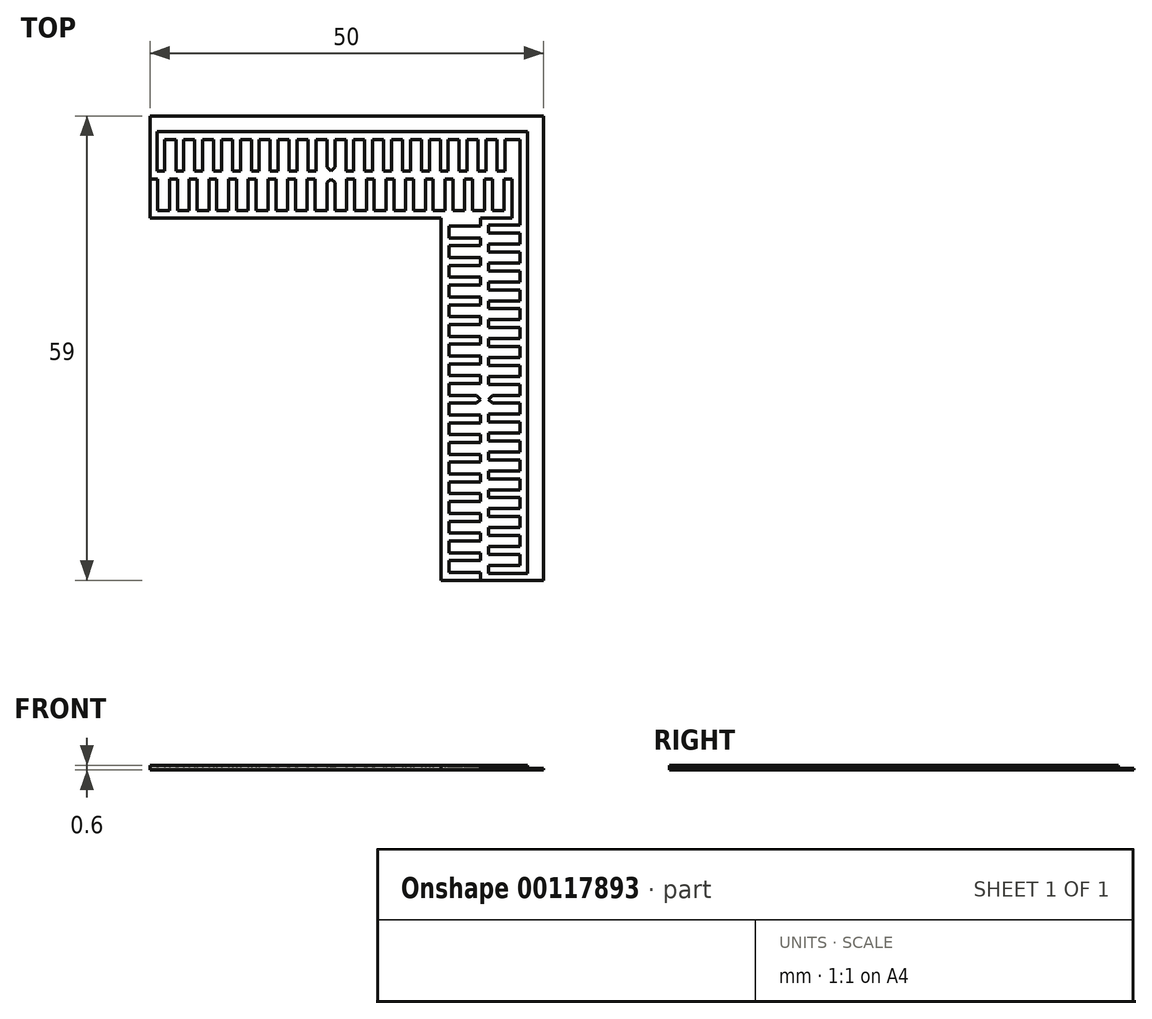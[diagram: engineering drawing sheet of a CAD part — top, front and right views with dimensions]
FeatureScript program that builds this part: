
annotation { "Feature Type Name" : "Feature", "Feature Type Description" : "" }
export const myFeature = defineFeature(function(context is Context, id is Id, definition is map)
    precondition{}
    {
        {
            assignVariable(context, id + "F0", {"name" : "pegThickness", "anyValue" : 0.4});
        }
        {
            var Q0;
            Q0=qCreatedBy(makeId("Top.planeOp"),FACE);
            var sketch = newSketch(context, id + "F1", { "sketchPlane" : qUnion([Q0])});
            skLineSegment(sketch, "E0.bottom", {"start": v(-0.5, 4) * mm, "end": v(0.5, 4) * mm});
            skLineSegment(sketch, "E0.top", {"start": v(-0.5, 0) * mm, "end": v(0.5, 0) * mm});
            skLineSegment(sketch, "E0.left", {"start": v(-0.5, 4) * mm, "end": v(-0.5, 0) * mm});
            skLineSegment(sketch, "E0.right", {"start": v(0.5, 4) * mm, "end": v(0.5, 0) * mm});
            skLineSegment(sketch, "E1.1.0.0", {"start": v(2, 0) * mm, "end": v(3, 0) * mm});
            skLineSegment(sketch, "E1.1.0.1", {"start": v(2, 4) * mm, "end": v(2, 0) * mm});
            skLineSegment(sketch, "E1.1.0.2", {"start": v(3, 4) * mm, "end": v(3, 0) * mm});
            skLineSegment(sketch, "E1.1.0.3", {"start": v(2, 4) * mm, "end": v(3, 4) * mm});
            skLineSegment(sketch, "E1.2.0.0", {"start": v(4.5, 0) * mm, "end": v(5.5, 0) * mm});
            skLineSegment(sketch, "E1.2.0.1", {"start": v(4.5, 4) * mm, "end": v(4.5, 0) * mm});
            skLineSegment(sketch, "E1.2.0.2", {"start": v(5.5, 4) * mm, "end": v(5.5, 0) * mm});
            skLineSegment(sketch, "E1.2.0.3", {"start": v(4.5, 4) * mm, "end": v(5.5, 4) * mm});
            skLineSegment(sketch, "E1.3.0.0", {"start": v(7, 0) * mm, "end": v(8, 0) * mm});
            skLineSegment(sketch, "E1.3.0.1", {"start": v(7, 4) * mm, "end": v(7, 0) * mm});
            skLineSegment(sketch, "E1.3.0.2", {"start": v(8, 4) * mm, "end": v(8, 0) * mm});
            skLineSegment(sketch, "E1.3.0.3", {"start": v(7, 4) * mm, "end": v(8, 4) * mm});
            skLineSegment(sketch, "E1.4.0.0", {"start": v(9.5, 0) * mm, "end": v(10.5, 0) * mm});
            skLineSegment(sketch, "E1.4.0.1", {"start": v(9.5, 4) * mm, "end": v(9.5, 0) * mm});
            skLineSegment(sketch, "E1.4.0.2", {"start": v(10.5, 4) * mm, "end": v(10.5, 0) * mm});
            skLineSegment(sketch, "E1.4.0.3", {"start": v(9.5, 4) * mm, "end": v(10.5, 4) * mm});
            skLineSegment(sketch, "E1.5.0.0", {"start": v(12, 0) * mm, "end": v(13, 0) * mm});
            skLineSegment(sketch, "E1.5.0.1", {"start": v(12, 4) * mm, "end": v(12, 0) * mm});
            skLineSegment(sketch, "E1.5.0.2", {"start": v(13, 4) * mm, "end": v(13, 0) * mm});
            skLineSegment(sketch, "E1.5.0.3", {"start": v(12, 4) * mm, "end": v(13, 4) * mm});
            skLineSegment(sketch, "E1.6.0.0", {"start": v(14.5, 0) * mm, "end": v(15.5, 0) * mm});
            skLineSegment(sketch, "E1.6.0.1", {"start": v(14.5, 4) * mm, "end": v(14.5, 0) * mm});
            skLineSegment(sketch, "E1.6.0.2", {"start": v(15.5, 4) * mm, "end": v(15.5, 0) * mm});
            skLineSegment(sketch, "E1.6.0.3", {"start": v(14.5, 4) * mm, "end": v(15.5, 4) * mm});
            skLineSegment(sketch, "E1.7.0.0", {"start": v(17, 0) * mm, "end": v(18, 0) * mm});
            skLineSegment(sketch, "E1.7.0.1", {"start": v(17, 4) * mm, "end": v(17, 0) * mm});
            skLineSegment(sketch, "E1.7.0.2", {"start": v(18, 4) * mm, "end": v(18, 0) * mm});
            skLineSegment(sketch, "E1.7.0.3", {"start": v(17, 4) * mm, "end": v(18, 4) * mm});
            skLineSegment(sketch, "E1.8.0.0", {"start": v(19.5, 0) * mm, "end": v(20.5, 0) * mm});
            skLineSegment(sketch, "E1.8.0.1", {"start": v(19.5, 4) * mm, "end": v(19.5, 0) * mm});
            skLineSegment(sketch, "E1.8.0.2", {"start": v(20.5, 4) * mm, "end": v(20.5, 0) * mm});
            skLineSegment(sketch, "E1.8.0.3", {"start": v(19.5, 4) * mm, "end": v(20.5, 4) * mm});
            skLineSegment(sketch, "E1.9.0.0", {"start": v(22, 0) * mm, "end": v(23, 0) * mm});
            skLineSegment(sketch, "E1.9.0.1", {"start": v(22, 4) * mm, "end": v(22, 0) * mm});
            skLineSegment(sketch, "E1.9.0.2", {"start": v(23, 4) * mm, "end": v(23, 0) * mm});
            skLineSegment(sketch, "E1.9.0.3", {"start": v(22, 4) * mm, "end": v(23, 4) * mm});
            skLineSegment(sketch, "E1.direction1", {"start": v(-0.5, 0) * mm, "end": v(2, 0) * mm, "construction": true});
            skLineSegment(sketch, "E2.1.0.0", {"start": v(-2, 4) * mm, "end": v(-2, 0) * mm});
            skLineSegment(sketch, "E2.1.0.1", {"start": v(-3, 4) * mm, "end": v(-3, 0) * mm});
            skLineSegment(sketch, "E2.1.0.2", {"start": v(-3, 0) * mm, "end": v(-2, 0) * mm});
            skLineSegment(sketch, "E2.1.0.3", {"start": v(-3, 4) * mm, "end": v(-2, 4) * mm});
            skLineSegment(sketch, "E2.2.0.0", {"start": v(-4.5, 4) * mm, "end": v(-4.5, 0) * mm});
            skLineSegment(sketch, "E2.2.0.1", {"start": v(-5.5, 4) * mm, "end": v(-5.5, 0) * mm});
            skLineSegment(sketch, "E2.2.0.2", {"start": v(-5.5, 0) * mm, "end": v(-4.5, 0) * mm});
            skLineSegment(sketch, "E2.2.0.3", {"start": v(-5.5, 4) * mm, "end": v(-4.5, 4) * mm});
            skLineSegment(sketch, "E2.3.0.0", {"start": v(-7, 4) * mm, "end": v(-7, 0) * mm});
            skLineSegment(sketch, "E2.3.0.1", {"start": v(-8, 4) * mm, "end": v(-8, 0) * mm});
            skLineSegment(sketch, "E2.3.0.2", {"start": v(-8, 0) * mm, "end": v(-7, 0) * mm});
            skLineSegment(sketch, "E2.3.0.3", {"start": v(-8, 4) * mm, "end": v(-7, 4) * mm});
            skLineSegment(sketch, "E2.4.0.0", {"start": v(-9.5, 4) * mm, "end": v(-9.5, 0) * mm});
            skLineSegment(sketch, "E2.4.0.1", {"start": v(-10.5, 4) * mm, "end": v(-10.5, 0) * mm});
            skLineSegment(sketch, "E2.4.0.2", {"start": v(-10.5, 0) * mm, "end": v(-9.5, 0) * mm});
            skLineSegment(sketch, "E2.4.0.3", {"start": v(-10.5, 4) * mm, "end": v(-9.5, 4) * mm});
            skLineSegment(sketch, "E2.5.0.0", {"start": v(-12, 4) * mm, "end": v(-12, 0) * mm});
            skLineSegment(sketch, "E2.5.0.1", {"start": v(-13, 4) * mm, "end": v(-13, 0) * mm});
            skLineSegment(sketch, "E2.5.0.2", {"start": v(-13, 0) * mm, "end": v(-12, 0) * mm});
            skLineSegment(sketch, "E2.5.0.3", {"start": v(-13, 4) * mm, "end": v(-12, 4) * mm});
            skLineSegment(sketch, "E2.6.0.0", {"start": v(-14.5, 4) * mm, "end": v(-14.5, 0) * mm});
            skLineSegment(sketch, "E2.6.0.1", {"start": v(-15.5, 4) * mm, "end": v(-15.5, 0) * mm});
            skLineSegment(sketch, "E2.6.0.2", {"start": v(-15.5, 0) * mm, "end": v(-14.5, 0) * mm});
            skLineSegment(sketch, "E2.6.0.3", {"start": v(-15.5, 4) * mm, "end": v(-14.5, 4) * mm});
            skLineSegment(sketch, "E2.7.0.0", {"start": v(-17, 4) * mm, "end": v(-17, 0) * mm});
            skLineSegment(sketch, "E2.7.0.1", {"start": v(-18, 4) * mm, "end": v(-18, 0) * mm});
            skLineSegment(sketch, "E2.7.0.2", {"start": v(-18, 0) * mm, "end": v(-17, 0) * mm});
            skLineSegment(sketch, "E2.7.0.3", {"start": v(-18, 4) * mm, "end": v(-17, 4) * mm});
            skLineSegment(sketch, "E2.8.0.0", {"start": v(-19.5, 4) * mm, "end": v(-19.5, 0) * mm});
            skLineSegment(sketch, "E2.8.0.1", {"start": v(-20.5, 4) * mm, "end": v(-20.5, 0) * mm});
            skLineSegment(sketch, "E2.8.0.2", {"start": v(-20.5, 0) * mm, "end": v(-19.5, 0) * mm});
            skLineSegment(sketch, "E2.8.0.3", {"start": v(-20.5, 4) * mm, "end": v(-19.5, 4) * mm});
            skLineSegment(sketch, "E2.9.0.0", {"start": v(-22, 4) * mm, "end": v(-22, 0) * mm});
            skLineSegment(sketch, "E2.9.0.1", {"start": v(-23, 4) * mm, "end": v(-23, 0) * mm});
            skLineSegment(sketch, "E2.9.0.2", {"start": v(-23, 0) * mm, "end": v(-22, 0) * mm});
            skLineSegment(sketch, "E2.9.0.3", {"start": v(-23, 4) * mm, "end": v(-22, 4) * mm});
            skLineSegment(sketch, "E2.direction1", {"start": v(-0.5, 0) * mm, "end": v(-3, 0) * mm, "construction": true});
            skLineSegment(sketch, "E3.bottom", {"start": v(-23, 0) * mm, "end": v(23, 0) * mm});
            skLineSegment(sketch, "E3.top", {"start": v(-23, -1) * mm, "end": v(23, -1) * mm});
            skLineSegment(sketch, "E3.left", {"start": v(-23, 0) * mm, "end": v(-23, -1) * mm});
            skLineSegment(sketch, "E3.right", {"start": v(23, 0) * mm, "end": v(23, -1) * mm});
            skSolve(sketch);
        }
        {
            var Q0;
            Q0=qSketchRegion(id+"F1",true);
            extrude(context, id + "F2", {"entities" : qUnion([Q0]), "depth" : (getVariable(context, 'pegThickness')) * mm});
        }
        {
            var Q0;
            Q0=qCreatedBy(makeId("Top.planeOp"),FACE);
            var sketch = newSketch(context, id + "F3", { "sketchPlane" : qUnion([Q0])});
            skLineSegment(sketch, "E4.bottom", {"start": v(-0.5, -5) * mm, "end": v(0.5, -5) * mm});
            skLineSegment(sketch, "E4.top", {"start": v(-0.5, -9) * mm, "end": v(0.5, -9) * mm});
            skLineSegment(sketch, "E4.left", {"start": v(-0.5, -5) * mm, "end": v(-0.5, -9) * mm});
            skLineSegment(sketch, "E4.right", {"start": v(0.5, -5) * mm, "end": v(0.5, -9) * mm});
            skLineSegment(sketch, "E5.1.0.0", {"start": v(1.9, -9) * mm, "end": v(2.9, -9) * mm});
            skLineSegment(sketch, "E5.1.0.1", {"start": v(1.9, -5) * mm, "end": v(1.9, -9) * mm});
            skLineSegment(sketch, "E5.1.0.2", {"start": v(2.9, -5) * mm, "end": v(2.9, -9) * mm});
            skLineSegment(sketch, "E5.1.0.3", {"start": v(1.9, -5) * mm, "end": v(2.9, -5) * mm});
            skLineSegment(sketch, "E5.2.0.0", {"start": v(4.3, -9) * mm, "end": v(5.3, -9) * mm});
            skLineSegment(sketch, "E5.2.0.1", {"start": v(4.3, -5) * mm, "end": v(4.3, -9) * mm});
            skLineSegment(sketch, "E5.2.0.2", {"start": v(5.3, -5) * mm, "end": v(5.3, -9) * mm});
            skLineSegment(sketch, "E5.2.0.3", {"start": v(4.3, -5) * mm, "end": v(5.3, -5) * mm});
            skLineSegment(sketch, "E5.3.0.0", {"start": v(6.7, -9) * mm, "end": v(7.7, -9) * mm});
            skLineSegment(sketch, "E5.3.0.1", {"start": v(6.7, -5) * mm, "end": v(6.7, -9) * mm});
            skLineSegment(sketch, "E5.3.0.2", {"start": v(7.7, -5) * mm, "end": v(7.7, -9) * mm});
            skLineSegment(sketch, "E5.3.0.3", {"start": v(6.7, -5) * mm, "end": v(7.7, -5) * mm});
            skLineSegment(sketch, "E5.4.0.0", {"start": v(9.1, -9) * mm, "end": v(10.1, -9) * mm});
            skLineSegment(sketch, "E5.4.0.1", {"start": v(9.1, -5) * mm, "end": v(9.1, -9) * mm});
            skLineSegment(sketch, "E5.4.0.2", {"start": v(10.1, -5) * mm, "end": v(10.1, -9) * mm});
            skLineSegment(sketch, "E5.4.0.3", {"start": v(9.1, -5) * mm, "end": v(10.1, -5) * mm});
            skLineSegment(sketch, "E5.5.0.0", {"start": v(11.5, -9) * mm, "end": v(12.5, -9) * mm});
            skLineSegment(sketch, "E5.5.0.1", {"start": v(11.5, -5) * mm, "end": v(11.5, -9) * mm});
            skLineSegment(sketch, "E5.5.0.2", {"start": v(12.5, -5) * mm, "end": v(12.5, -9) * mm});
            skLineSegment(sketch, "E5.5.0.3", {"start": v(11.5, -5) * mm, "end": v(12.5, -5) * mm});
            skLineSegment(sketch, "E5.6.0.0", {"start": v(13.9, -9) * mm, "end": v(14.9, -9) * mm});
            skLineSegment(sketch, "E5.6.0.1", {"start": v(13.9, -5) * mm, "end": v(13.9, -9) * mm});
            skLineSegment(sketch, "E5.6.0.2", {"start": v(14.9, -5) * mm, "end": v(14.9, -9) * mm});
            skLineSegment(sketch, "E5.6.0.3", {"start": v(13.9, -5) * mm, "end": v(14.9, -5) * mm});
            skLineSegment(sketch, "E5.7.0.0", {"start": v(16.3, -9) * mm, "end": v(17.3, -9) * mm});
            skLineSegment(sketch, "E5.7.0.1", {"start": v(16.3, -5) * mm, "end": v(16.3, -9) * mm});
            skLineSegment(sketch, "E5.7.0.2", {"start": v(17.3, -5) * mm, "end": v(17.3, -9) * mm});
            skLineSegment(sketch, "E5.7.0.3", {"start": v(16.3, -5) * mm, "end": v(17.3, -5) * mm});
            skLineSegment(sketch, "E5.8.0.0", {"start": v(18.7, -9) * mm, "end": v(19.7, -9) * mm});
            skLineSegment(sketch, "E5.8.0.1", {"start": v(18.7, -5) * mm, "end": v(18.7, -9) * mm});
            skLineSegment(sketch, "E5.8.0.2", {"start": v(19.7, -5) * mm, "end": v(19.7, -9) * mm});
            skLineSegment(sketch, "E5.8.0.3", {"start": v(18.7, -5) * mm, "end": v(19.7, -5) * mm});
            skLineSegment(sketch, "E5.9.0.0", {"start": v(21.1, -9) * mm, "end": v(22.1, -9) * mm});
            skLineSegment(sketch, "E5.9.0.1", {"start": v(21.1, -5) * mm, "end": v(21.1, -9) * mm});
            skLineSegment(sketch, "E5.9.0.2", {"start": v(22.1, -5) * mm, "end": v(22.1, -9) * mm});
            skLineSegment(sketch, "E5.9.0.3", {"start": v(21.1, -5) * mm, "end": v(22.1, -5) * mm});
            skLineSegment(sketch, "E5.direction1", {"start": v(-0.5, -9) * mm, "end": v(1.9, -9) * mm, "construction": true});
            skLineSegment(sketch, "E6.1.0.0", {"start": v(-1.9, -5) * mm, "end": v(-1.9, -9) * mm});
            skLineSegment(sketch, "E6.1.0.1", {"start": v(-2.9, -5) * mm, "end": v(-2.9, -9) * mm});
            skLineSegment(sketch, "E6.1.0.2", {"start": v(-2.9, -9) * mm, "end": v(-1.9, -9) * mm});
            skLineSegment(sketch, "E6.1.0.3", {"start": v(-2.9, -5) * mm, "end": v(-1.9, -5) * mm});
            skLineSegment(sketch, "E6.2.0.0", {"start": v(-4.3, -5) * mm, "end": v(-4.3, -9) * mm});
            skLineSegment(sketch, "E6.2.0.1", {"start": v(-5.3, -5) * mm, "end": v(-5.3, -9) * mm});
            skLineSegment(sketch, "E6.2.0.2", {"start": v(-5.3, -9) * mm, "end": v(-4.3, -9) * mm});
            skLineSegment(sketch, "E6.2.0.3", {"start": v(-5.3, -5) * mm, "end": v(-4.3, -5) * mm});
            skLineSegment(sketch, "E6.3.0.0", {"start": v(-6.7, -5) * mm, "end": v(-6.7, -9) * mm});
            skLineSegment(sketch, "E6.3.0.1", {"start": v(-7.7, -5) * mm, "end": v(-7.7, -9) * mm});
            skLineSegment(sketch, "E6.3.0.2", {"start": v(-7.7, -9) * mm, "end": v(-6.7, -9) * mm});
            skLineSegment(sketch, "E6.3.0.3", {"start": v(-7.7, -5) * mm, "end": v(-6.7, -5) * mm});
            skLineSegment(sketch, "E6.4.0.0", {"start": v(-9.1, -5) * mm, "end": v(-9.1, -9) * mm});
            skLineSegment(sketch, "E6.4.0.1", {"start": v(-10.1, -5) * mm, "end": v(-10.1, -9) * mm});
            skLineSegment(sketch, "E6.4.0.2", {"start": v(-10.1, -9) * mm, "end": v(-9.1, -9) * mm});
            skLineSegment(sketch, "E6.4.0.3", {"start": v(-10.1, -5) * mm, "end": v(-9.1, -5) * mm});
            skLineSegment(sketch, "E6.5.0.0", {"start": v(-11.5, -5) * mm, "end": v(-11.5, -9) * mm});
            skLineSegment(sketch, "E6.5.0.1", {"start": v(-12.5, -5) * mm, "end": v(-12.5, -9) * mm});
            skLineSegment(sketch, "E6.5.0.2", {"start": v(-12.5, -9) * mm, "end": v(-11.5, -9) * mm});
            skLineSegment(sketch, "E6.5.0.3", {"start": v(-12.5, -5) * mm, "end": v(-11.5, -5) * mm});
            skLineSegment(sketch, "E6.6.0.0", {"start": v(-13.9, -5) * mm, "end": v(-13.9, -9) * mm});
            skLineSegment(sketch, "E6.6.0.1", {"start": v(-14.9, -5) * mm, "end": v(-14.9, -9) * mm});
            skLineSegment(sketch, "E6.6.0.2", {"start": v(-14.9, -9) * mm, "end": v(-13.9, -9) * mm});
            skLineSegment(sketch, "E6.6.0.3", {"start": v(-14.9, -5) * mm, "end": v(-13.9, -5) * mm});
            skLineSegment(sketch, "E6.7.0.0", {"start": v(-16.3, -5) * mm, "end": v(-16.3, -9) * mm});
            skLineSegment(sketch, "E6.7.0.1", {"start": v(-17.3, -5) * mm, "end": v(-17.3, -9) * mm});
            skLineSegment(sketch, "E6.7.0.2", {"start": v(-17.3, -9) * mm, "end": v(-16.3, -9) * mm});
            skLineSegment(sketch, "E6.7.0.3", {"start": v(-17.3, -5) * mm, "end": v(-16.3, -5) * mm});
            skLineSegment(sketch, "E6.8.0.0", {"start": v(-18.7, -5) * mm, "end": v(-18.7, -9) * mm});
            skLineSegment(sketch, "E6.8.0.1", {"start": v(-19.7, -5) * mm, "end": v(-19.7, -9) * mm});
            skLineSegment(sketch, "E6.8.0.2", {"start": v(-19.7, -9) * mm, "end": v(-18.7, -9) * mm});
            skLineSegment(sketch, "E6.8.0.3", {"start": v(-19.7, -5) * mm, "end": v(-18.7, -5) * mm});
            skLineSegment(sketch, "E6.9.0.0", {"start": v(-21.1, -5) * mm, "end": v(-21.1, -9) * mm});
            skLineSegment(sketch, "E6.9.0.1", {"start": v(-22.1, -5) * mm, "end": v(-22.1, -9) * mm});
            skLineSegment(sketch, "E6.9.0.2", {"start": v(-22.1, -9) * mm, "end": v(-21.1, -9) * mm});
            skLineSegment(sketch, "E6.9.0.3", {"start": v(-22.1, -5) * mm, "end": v(-21.1, -5) * mm});
            skLineSegment(sketch, "E6.direction1", {"start": v(-0.5, -9) * mm, "end": v(-2.9, -9) * mm, "construction": true});
            skLineSegment(sketch, "E7.bottom", {"start": v(-22.1, -9) * mm, "end": v(22.1, -9) * mm});
            skLineSegment(sketch, "E7.top", {"start": v(-22.1, -10) * mm, "end": v(22.1, -10) * mm});
            skLineSegment(sketch, "E7.left", {"start": v(-22.1, -9) * mm, "end": v(-22.1, -10) * mm});
            skLineSegment(sketch, "E7.right", {"start": v(22.1, -9) * mm, "end": v(22.1, -10) * mm});
            skPoint(sketch, "E8", {"position": v(0, -5) * mm});
            skSolve(sketch);
        }
        {
            var Q0;
            Q0=qSketchRegion(id+"F3",true);
            extrude(context, id + "F4", {"entities" : qUnion([Q0]), "depth" : (getVariable(context, 'pegThickness')) * mm});
        }
        {
            var Q0;
            Q0=makeQuery(id+"F4.opExtrude","SWEPT_BODY",BODY,{"disambiguationData":[OSD([sQuery(id+"F3.wireOp",EDGE,"E4.bottom"),sQuery(id+"F3.wireOp",EDGE,"E4.left"),sQuery(id+"F3.wireOp",EDGE,"E4.right"),sQuery(id+"F3.wireOp",EDGE,"E5.1.0.1"),sQuery(id+"F3.wireOp",EDGE,"E5.1.0.2"),sQuery(id+"F3.wireOp",EDGE,"E5.1.0.3"),sQuery(id+"F3.wireOp",EDGE,"E5.2.0.1"),sQuery(id+"F3.wireOp",EDGE,"E5.2.0.2"),sQuery(id+"F3.wireOp",EDGE,"E5.2.0.3"),sQuery(id+"F3.wireOp",EDGE,"E5.3.0.1"),sQuery(id+"F3.wireOp",EDGE,"E5.3.0.2"),sQuery(id+"F3.wireOp",EDGE,"E5.3.0.3"),sQuery(id+"F3.wireOp",EDGE,"E5.4.0.1"),sQuery(id+"F3.wireOp",EDGE,"E5.4.0.2"),sQuery(id+"F3.wireOp",EDGE,"E5.4.0.3"),sQuery(id+"F3.wireOp",EDGE,"E5.5.0.1"),sQuery(id+"F3.wireOp",EDGE,"E5.5.0.2"),sQuery(id+"F3.wireOp",EDGE,"E5.5.0.3"),sQuery(id+"F3.wireOp",EDGE,"E5.6.0.1"),sQuery(id+"F3.wireOp",EDGE,"E5.6.0.2"),sQuery(id+"F3.wireOp",EDGE,"E5.6.0.3"),sQuery(id+"F3.wireOp",EDGE,"E5.7.0.1"),sQuery(id+"F3.wireOp",EDGE,"E5.7.0.2"),sQuery(id+"F3.wireOp",EDGE,"E5.7.0.3"),sQuery(id+"F3.wireOp",EDGE,"E5.8.0.1"),sQuery(id+"F3.wireOp",EDGE,"E5.8.0.2"),sQuery(id+"F3.wireOp",EDGE,"E5.8.0.3"),sQuery(id+"F3.wireOp",EDGE,"E5.9.0.1"),sQuery(id+"F3.wireOp",EDGE,"E5.9.0.2"),sQuery(id+"F3.wireOp",EDGE,"E5.9.0.3"),sQuery(id+"F3.wireOp",EDGE,"E6.1.0.0"),sQuery(id+"F3.wireOp",EDGE,"E6.1.0.1"),sQuery(id+"F3.wireOp",EDGE,"E6.1.0.3"),sQuery(id+"F3.wireOp",EDGE,"E6.2.0.0"),sQuery(id+"F3.wireOp",EDGE,"E6.2.0.1"),sQuery(id+"F3.wireOp",EDGE,"E6.2.0.3"),sQuery(id+"F3.wireOp",EDGE,"E6.3.0.0"),sQuery(id+"F3.wireOp",EDGE,"E6.3.0.1"),sQuery(id+"F3.wireOp",EDGE,"E6.3.0.3"),sQuery(id+"F3.wireOp",EDGE,"E6.4.0.0"),sQuery(id+"F3.wireOp",EDGE,"E6.4.0.1"),sQuery(id+"F3.wireOp",EDGE,"E6.4.0.3"),sQuery(id+"F3.wireOp",EDGE,"E6.5.0.0"),sQuery(id+"F3.wireOp",EDGE,"E6.5.0.1"),sQuery(id+"F3.wireOp",EDGE,"E6.5.0.3"),sQuery(id+"F3.wireOp",EDGE,"E6.6.0.0"),sQuery(id+"F3.wireOp",EDGE,"E6.6.0.1"),sQuery(id+"F3.wireOp",EDGE,"E6.6.0.3"),sQuery(id+"F3.wireOp",EDGE,"E6.7.0.0"),sQuery(id+"F3.wireOp",EDGE,"E6.7.0.1"),sQuery(id+"F3.wireOp",EDGE,"E6.7.0.3"),sQuery(id+"F3.wireOp",EDGE,"E6.8.0.0"),sQuery(id+"F3.wireOp",EDGE,"E6.8.0.1"),sQuery(id+"F3.wireOp",EDGE,"E6.8.0.3"),sQuery(id+"F3.wireOp",EDGE,"E6.9.0.0"),sQuery(id+"F3.wireOp",EDGE,"E6.9.0.1"),sQuery(id+"F3.wireOp",EDGE,"E6.9.0.3"),sQuery(id+"F3.wireOp",EDGE,"E7.bottom"),sQuery(id+"F3.wireOp",EDGE,"E7.top"),sQuery(id+"F3.wireOp",EDGE,"E7.left"),sQuery(id+"F3.wireOp",EDGE,"E7.right")])]});
            var Q1;
            Q1=qCreatedBy(makeId("Front.planeOp"),FACE);
            mirror(context, id + "F5", {"entities" : qUnion([Q0]), "mirrorPlane" : qUnion([Q1])});
        }
        {
            var Q0;
            Q0=makeQuery(id+"F4.opExtrude","SWEPT_BODY",BODY,{"disambiguationData":[OSD([sQuery(id+"F3.wireOp",EDGE,"E4.bottom"),sQuery(id+"F3.wireOp",EDGE,"E4.left"),sQuery(id+"F3.wireOp",EDGE,"E4.right"),sQuery(id+"F3.wireOp",EDGE,"E5.1.0.1"),sQuery(id+"F3.wireOp",EDGE,"E5.1.0.2"),sQuery(id+"F3.wireOp",EDGE,"E5.1.0.3"),sQuery(id+"F3.wireOp",EDGE,"E5.2.0.1"),sQuery(id+"F3.wireOp",EDGE,"E5.2.0.2"),sQuery(id+"F3.wireOp",EDGE,"E5.2.0.3"),sQuery(id+"F3.wireOp",EDGE,"E5.3.0.1"),sQuery(id+"F3.wireOp",EDGE,"E5.3.0.2"),sQuery(id+"F3.wireOp",EDGE,"E5.3.0.3"),sQuery(id+"F3.wireOp",EDGE,"E5.4.0.1"),sQuery(id+"F3.wireOp",EDGE,"E5.4.0.2"),sQuery(id+"F3.wireOp",EDGE,"E5.4.0.3"),sQuery(id+"F3.wireOp",EDGE,"E5.5.0.1"),sQuery(id+"F3.wireOp",EDGE,"E5.5.0.2"),sQuery(id+"F3.wireOp",EDGE,"E5.5.0.3"),sQuery(id+"F3.wireOp",EDGE,"E5.6.0.1"),sQuery(id+"F3.wireOp",EDGE,"E5.6.0.2"),sQuery(id+"F3.wireOp",EDGE,"E5.6.0.3"),sQuery(id+"F3.wireOp",EDGE,"E5.7.0.1"),sQuery(id+"F3.wireOp",EDGE,"E5.7.0.2"),sQuery(id+"F3.wireOp",EDGE,"E5.7.0.3"),sQuery(id+"F3.wireOp",EDGE,"E5.8.0.1"),sQuery(id+"F3.wireOp",EDGE,"E5.8.0.2"),sQuery(id+"F3.wireOp",EDGE,"E5.8.0.3"),sQuery(id+"F3.wireOp",EDGE,"E5.9.0.1"),sQuery(id+"F3.wireOp",EDGE,"E5.9.0.2"),sQuery(id+"F3.wireOp",EDGE,"E5.9.0.3"),sQuery(id+"F3.wireOp",EDGE,"E6.1.0.0"),sQuery(id+"F3.wireOp",EDGE,"E6.1.0.1"),sQuery(id+"F3.wireOp",EDGE,"E6.1.0.3"),sQuery(id+"F3.wireOp",EDGE,"E6.2.0.0"),sQuery(id+"F3.wireOp",EDGE,"E6.2.0.1"),sQuery(id+"F3.wireOp",EDGE,"E6.2.0.3"),sQuery(id+"F3.wireOp",EDGE,"E6.3.0.0"),sQuery(id+"F3.wireOp",EDGE,"E6.3.0.1"),sQuery(id+"F3.wireOp",EDGE,"E6.3.0.3"),sQuery(id+"F3.wireOp",EDGE,"E6.4.0.0"),sQuery(id+"F3.wireOp",EDGE,"E6.4.0.1"),sQuery(id+"F3.wireOp",EDGE,"E6.4.0.3"),sQuery(id+"F3.wireOp",EDGE,"E6.5.0.0"),sQuery(id+"F3.wireOp",EDGE,"E6.5.0.1"),sQuery(id+"F3.wireOp",EDGE,"E6.5.0.3"),sQuery(id+"F3.wireOp",EDGE,"E6.6.0.0"),sQuery(id+"F3.wireOp",EDGE,"E6.6.0.1"),sQuery(id+"F3.wireOp",EDGE,"E6.6.0.3"),sQuery(id+"F3.wireOp",EDGE,"E6.7.0.0"),sQuery(id+"F3.wireOp",EDGE,"E6.7.0.1"),sQuery(id+"F3.wireOp",EDGE,"E6.7.0.3"),sQuery(id+"F3.wireOp",EDGE,"E6.8.0.0"),sQuery(id+"F3.wireOp",EDGE,"E6.8.0.1"),sQuery(id+"F3.wireOp",EDGE,"E6.8.0.3"),sQuery(id+"F3.wireOp",EDGE,"E6.9.0.0"),sQuery(id+"F3.wireOp",EDGE,"E6.9.0.1"),sQuery(id+"F3.wireOp",EDGE,"E6.9.0.3"),sQuery(id+"F3.wireOp",EDGE,"E7.bottom"),sQuery(id+"F3.wireOp",EDGE,"E7.top"),sQuery(id+"F3.wireOp",EDGE,"E7.left"),sQuery(id+"F3.wireOp",EDGE,"E7.right")])]});
            deleteBodies(context, id + "F6", {"entities" : qUnion([Q0])});
        }
        {
            var Q0;
            Q0=makeQuery(id+"F5.opPattern","COPY",EDGE,{"derivedFrom":makeQuery(id+"F4.opExtrude","SWEPT_EDGE",EDGE,{"disambiguationData":[OSD([sQuery(id+"F3.wireOp",EDGE,"E4.bottom"),sQuery(id+"F3.wireOp",EDGE,"E4.left")])]}),"instanceName":"1"});
            var Q1;
            Q1=makeQuery(id+"F5.opPattern","COPY",EDGE,{"derivedFrom":makeQuery(id+"F4.opExtrude","SWEPT_EDGE",EDGE,{"disambiguationData":[OSD([sQuery(id+"F3.wireOp",EDGE,"E4.bottom"),sQuery(id+"F3.wireOp",EDGE,"E4.right")])]}),"instanceName":"1"});
            var Q2;
            Q2=makeQuery(id+"F2.opExtrude","SWEPT_EDGE",EDGE,{"disambiguationData":[OSD([sQuery(id+"F1.wireOp",EDGE,"E0.bottom"),sQuery(id+"F1.wireOp",EDGE,"E0.right")])]});
            var Q3;
            Q3=makeQuery(id+"F2.opExtrude","SWEPT_EDGE",EDGE,{"disambiguationData":[OSD([sQuery(id+"F1.wireOp",EDGE,"E0.bottom"),sQuery(id+"F1.wireOp",EDGE,"E0.left")])]});
            chamfer(context, id + "F7", {"entities" : qUnion([Q0, Q1, Q2, Q3]), "width" : 0.5 * mm, "tangentPropagation" : true});
        }
        {
            var Q0;
            Q0=makeQuery(id+"F2.opExtrude","SWEPT_BODY",BODY,{"disambiguationData":[OSD([sQuery(id+"F1.wireOp",EDGE,"E0.bottom"),sQuery(id+"F1.wireOp",EDGE,"E0.left"),sQuery(id+"F1.wireOp",EDGE,"E0.right"),sQuery(id+"F1.wireOp",EDGE,"E1.1.0.1"),sQuery(id+"F1.wireOp",EDGE,"E1.1.0.2"),sQuery(id+"F1.wireOp",EDGE,"E1.1.0.3"),sQuery(id+"F1.wireOp",EDGE,"E1.2.0.1"),sQuery(id+"F1.wireOp",EDGE,"E1.2.0.2"),sQuery(id+"F1.wireOp",EDGE,"E1.2.0.3"),sQuery(id+"F1.wireOp",EDGE,"E1.3.0.1"),sQuery(id+"F1.wireOp",EDGE,"E1.3.0.2"),sQuery(id+"F1.wireOp",EDGE,"E1.3.0.3"),sQuery(id+"F1.wireOp",EDGE,"E1.4.0.1"),sQuery(id+"F1.wireOp",EDGE,"E1.4.0.2"),sQuery(id+"F1.wireOp",EDGE,"E1.4.0.3"),sQuery(id+"F1.wireOp",EDGE,"E1.5.0.1"),sQuery(id+"F1.wireOp",EDGE,"E1.5.0.2"),sQuery(id+"F1.wireOp",EDGE,"E1.5.0.3"),sQuery(id+"F1.wireOp",EDGE,"E1.6.0.1"),sQuery(id+"F1.wireOp",EDGE,"E1.6.0.2"),sQuery(id+"F1.wireOp",EDGE,"E1.6.0.3"),sQuery(id+"F1.wireOp",EDGE,"E1.7.0.1"),sQuery(id+"F1.wireOp",EDGE,"E1.7.0.2"),sQuery(id+"F1.wireOp",EDGE,"E1.7.0.3"),sQuery(id+"F1.wireOp",EDGE,"E1.8.0.1"),sQuery(id+"F1.wireOp",EDGE,"E1.8.0.2"),sQuery(id+"F1.wireOp",EDGE,"E1.8.0.3"),sQuery(id+"F1.wireOp",EDGE,"E1.9.0.1"),sQuery(id+"F1.wireOp",EDGE,"E1.9.0.2"),sQuery(id+"F1.wireOp",EDGE,"E1.9.0.3"),sQuery(id+"F1.wireOp",EDGE,"E2.1.0.0"),sQuery(id+"F1.wireOp",EDGE,"E2.1.0.1"),sQuery(id+"F1.wireOp",EDGE,"E2.1.0.3"),sQuery(id+"F1.wireOp",EDGE,"E2.2.0.0"),sQuery(id+"F1.wireOp",EDGE,"E2.2.0.1"),sQuery(id+"F1.wireOp",EDGE,"E2.2.0.3"),sQuery(id+"F1.wireOp",EDGE,"E2.3.0.0"),sQuery(id+"F1.wireOp",EDGE,"E2.3.0.1"),sQuery(id+"F1.wireOp",EDGE,"E2.3.0.3"),sQuery(id+"F1.wireOp",EDGE,"E2.4.0.0"),sQuery(id+"F1.wireOp",EDGE,"E2.4.0.1"),sQuery(id+"F1.wireOp",EDGE,"E2.4.0.3"),sQuery(id+"F1.wireOp",EDGE,"E2.5.0.0"),sQuery(id+"F1.wireOp",EDGE,"E2.5.0.1"),sQuery(id+"F1.wireOp",EDGE,"E2.5.0.3"),sQuery(id+"F1.wireOp",EDGE,"E2.6.0.0"),sQuery(id+"F1.wireOp",EDGE,"E2.6.0.1"),sQuery(id+"F1.wireOp",EDGE,"E2.6.0.3"),sQuery(id+"F1.wireOp",EDGE,"E2.7.0.0"),sQuery(id+"F1.wireOp",EDGE,"E2.7.0.1"),sQuery(id+"F1.wireOp",EDGE,"E2.7.0.3"),sQuery(id+"F1.wireOp",EDGE,"E2.8.0.0"),sQuery(id+"F1.wireOp",EDGE,"E2.8.0.1"),sQuery(id+"F1.wireOp",EDGE,"E2.8.0.3"),sQuery(id+"F1.wireOp",EDGE,"E2.9.0.0"),sQuery(id+"F1.wireOp",EDGE,"E2.9.0.1"),sQuery(id+"F1.wireOp",EDGE,"E2.9.0.3"),sQuery(id+"F1.wireOp",EDGE,"E3.bottom"),sQuery(id+"F1.wireOp",EDGE,"E3.top"),sQuery(id+"F1.wireOp",EDGE,"E3.left"),sQuery(id+"F1.wireOp",EDGE,"E3.right")])]});
            var Q1;
            Q1=makeQuery(id+"F2.opExtrude","SWEPT_EDGE",EDGE,{"disambiguationData":[OSD([sQuery(id+"F1.wireOp",EDGE,"E3.top"),sQuery(id+"F1.wireOp",EDGE,"E3.left")])]});
            transform(context, id + "F8", {"entities" : qUnion([Q0]), "transformType" : TransformType.ROTATION, "transformAxis" : qUnion([Q1]), "angle" : 90 * degree, "makeCopy" : true});
        }
        {
            var Q0;
            Q0=makeQuery(id+"F5.opPattern","COPY",BODY,{"derivedFrom":makeQuery(id+"F4.opExtrude","SWEPT_BODY",BODY,{"disambiguationData":[OSD([sQuery(id+"F3.wireOp",EDGE,"E4.bottom"),sQuery(id+"F3.wireOp",EDGE,"E4.left"),sQuery(id+"F3.wireOp",EDGE,"E4.right"),sQuery(id+"F3.wireOp",EDGE,"E5.1.0.1"),sQuery(id+"F3.wireOp",EDGE,"E5.1.0.2"),sQuery(id+"F3.wireOp",EDGE,"E5.1.0.3"),sQuery(id+"F3.wireOp",EDGE,"E5.2.0.1"),sQuery(id+"F3.wireOp",EDGE,"E5.2.0.2"),sQuery(id+"F3.wireOp",EDGE,"E5.2.0.3"),sQuery(id+"F3.wireOp",EDGE,"E5.3.0.1"),sQuery(id+"F3.wireOp",EDGE,"E5.3.0.2"),sQuery(id+"F3.wireOp",EDGE,"E5.3.0.3"),sQuery(id+"F3.wireOp",EDGE,"E5.4.0.1"),sQuery(id+"F3.wireOp",EDGE,"E5.4.0.2"),sQuery(id+"F3.wireOp",EDGE,"E5.4.0.3"),sQuery(id+"F3.wireOp",EDGE,"E5.5.0.1"),sQuery(id+"F3.wireOp",EDGE,"E5.5.0.2"),sQuery(id+"F3.wireOp",EDGE,"E5.5.0.3"),sQuery(id+"F3.wireOp",EDGE,"E5.6.0.1"),sQuery(id+"F3.wireOp",EDGE,"E5.6.0.2"),sQuery(id+"F3.wireOp",EDGE,"E5.6.0.3"),sQuery(id+"F3.wireOp",EDGE,"E5.7.0.1"),sQuery(id+"F3.wireOp",EDGE,"E5.7.0.2"),sQuery(id+"F3.wireOp",EDGE,"E5.7.0.3"),sQuery(id+"F3.wireOp",EDGE,"E5.8.0.1"),sQuery(id+"F3.wireOp",EDGE,"E5.8.0.2"),sQuery(id+"F3.wireOp",EDGE,"E5.8.0.3"),sQuery(id+"F3.wireOp",EDGE,"E5.9.0.1"),sQuery(id+"F3.wireOp",EDGE,"E5.9.0.2"),sQuery(id+"F3.wireOp",EDGE,"E5.9.0.3"),sQuery(id+"F3.wireOp",EDGE,"E6.1.0.0"),sQuery(id+"F3.wireOp",EDGE,"E6.1.0.1"),sQuery(id+"F3.wireOp",EDGE,"E6.1.0.3"),sQuery(id+"F3.wireOp",EDGE,"E6.2.0.0"),sQuery(id+"F3.wireOp",EDGE,"E6.2.0.1"),sQuery(id+"F3.wireOp",EDGE,"E6.2.0.3"),sQuery(id+"F3.wireOp",EDGE,"E6.3.0.0"),sQuery(id+"F3.wireOp",EDGE,"E6.3.0.1"),sQuery(id+"F3.wireOp",EDGE,"E6.3.0.3"),sQuery(id+"F3.wireOp",EDGE,"E6.4.0.0"),sQuery(id+"F3.wireOp",EDGE,"E6.4.0.1"),sQuery(id+"F3.wireOp",EDGE,"E6.4.0.3"),sQuery(id+"F3.wireOp",EDGE,"E6.5.0.0"),sQuery(id+"F3.wireOp",EDGE,"E6.5.0.1"),sQuery(id+"F3.wireOp",EDGE,"E6.5.0.3"),sQuery(id+"F3.wireOp",EDGE,"E6.6.0.0"),sQuery(id+"F3.wireOp",EDGE,"E6.6.0.1"),sQuery(id+"F3.wireOp",EDGE,"E6.6.0.3"),sQuery(id+"F3.wireOp",EDGE,"E6.7.0.0"),sQuery(id+"F3.wireOp",EDGE,"E6.7.0.1"),sQuery(id+"F3.wireOp",EDGE,"E6.7.0.3"),sQuery(id+"F3.wireOp",EDGE,"E6.8.0.0"),sQuery(id+"F3.wireOp",EDGE,"E6.8.0.1"),sQuery(id+"F3.wireOp",EDGE,"E6.8.0.3"),sQuery(id+"F3.wireOp",EDGE,"E6.9.0.0"),sQuery(id+"F3.wireOp",EDGE,"E6.9.0.1"),sQuery(id+"F3.wireOp",EDGE,"E6.9.0.3"),sQuery(id+"F3.wireOp",EDGE,"E7.bottom"),sQuery(id+"F3.wireOp",EDGE,"E7.top"),sQuery(id+"F3.wireOp",EDGE,"E7.left"),sQuery(id+"F3.wireOp",EDGE,"E7.right")])]}),"instanceName":"1"});
            var Q1;
            Q1=makeQuery(id+"F2.opExtrude","SWEPT_EDGE",EDGE,{"disambiguationData":[OSD([sQuery(id+"F1.wireOp",EDGE,"E3.top"),sQuery(id+"F1.wireOp",EDGE,"E3.left")])]});
            transform(context, id + "F9", {"entities" : qUnion([Q0]), "transformType" : TransformType.ROTATION, "transformAxis" : qUnion([Q1]), "angle" : 90 * degree, "makeCopy" : true});
        }
        {
            var Q0;
            Q0=makeQuery(id+"F8.opPattern","COPY",BODY,{"derivedFrom":makeQuery(id+"F2.opExtrude","SWEPT_BODY",BODY,{"disambiguationData":[OSD([sQuery(id+"F1.wireOp",EDGE,"E0.bottom"),sQuery(id+"F1.wireOp",EDGE,"E0.left"),sQuery(id+"F1.wireOp",EDGE,"E0.right"),sQuery(id+"F1.wireOp",EDGE,"E1.1.0.1"),sQuery(id+"F1.wireOp",EDGE,"E1.1.0.2"),sQuery(id+"F1.wireOp",EDGE,"E1.1.0.3"),sQuery(id+"F1.wireOp",EDGE,"E1.2.0.1"),sQuery(id+"F1.wireOp",EDGE,"E1.2.0.2"),sQuery(id+"F1.wireOp",EDGE,"E1.2.0.3"),sQuery(id+"F1.wireOp",EDGE,"E1.3.0.1"),sQuery(id+"F1.wireOp",EDGE,"E1.3.0.2"),sQuery(id+"F1.wireOp",EDGE,"E1.3.0.3"),sQuery(id+"F1.wireOp",EDGE,"E1.4.0.1"),sQuery(id+"F1.wireOp",EDGE,"E1.4.0.2"),sQuery(id+"F1.wireOp",EDGE,"E1.4.0.3"),sQuery(id+"F1.wireOp",EDGE,"E1.5.0.1"),sQuery(id+"F1.wireOp",EDGE,"E1.5.0.2"),sQuery(id+"F1.wireOp",EDGE,"E1.5.0.3"),sQuery(id+"F1.wireOp",EDGE,"E1.6.0.1"),sQuery(id+"F1.wireOp",EDGE,"E1.6.0.2"),sQuery(id+"F1.wireOp",EDGE,"E1.6.0.3"),sQuery(id+"F1.wireOp",EDGE,"E1.7.0.1"),sQuery(id+"F1.wireOp",EDGE,"E1.7.0.2"),sQuery(id+"F1.wireOp",EDGE,"E1.7.0.3"),sQuery(id+"F1.wireOp",EDGE,"E1.8.0.1"),sQuery(id+"F1.wireOp",EDGE,"E1.8.0.2"),sQuery(id+"F1.wireOp",EDGE,"E1.8.0.3"),sQuery(id+"F1.wireOp",EDGE,"E1.9.0.1"),sQuery(id+"F1.wireOp",EDGE,"E1.9.0.2"),sQuery(id+"F1.wireOp",EDGE,"E1.9.0.3"),sQuery(id+"F1.wireOp",EDGE,"E2.1.0.0"),sQuery(id+"F1.wireOp",EDGE,"E2.1.0.1"),sQuery(id+"F1.wireOp",EDGE,"E2.1.0.3"),sQuery(id+"F1.wireOp",EDGE,"E2.2.0.0"),sQuery(id+"F1.wireOp",EDGE,"E2.2.0.1"),sQuery(id+"F1.wireOp",EDGE,"E2.2.0.3"),sQuery(id+"F1.wireOp",EDGE,"E2.3.0.0"),sQuery(id+"F1.wireOp",EDGE,"E2.3.0.1"),sQuery(id+"F1.wireOp",EDGE,"E2.3.0.3"),sQuery(id+"F1.wireOp",EDGE,"E2.4.0.0"),sQuery(id+"F1.wireOp",EDGE,"E2.4.0.1"),sQuery(id+"F1.wireOp",EDGE,"E2.4.0.3"),sQuery(id+"F1.wireOp",EDGE,"E2.5.0.0"),sQuery(id+"F1.wireOp",EDGE,"E2.5.0.1"),sQuery(id+"F1.wireOp",EDGE,"E2.5.0.3"),sQuery(id+"F1.wireOp",EDGE,"E2.6.0.0"),sQuery(id+"F1.wireOp",EDGE,"E2.6.0.1"),sQuery(id+"F1.wireOp",EDGE,"E2.6.0.3"),sQuery(id+"F1.wireOp",EDGE,"E2.7.0.0"),sQuery(id+"F1.wireOp",EDGE,"E2.7.0.1"),sQuery(id+"F1.wireOp",EDGE,"E2.7.0.3"),sQuery(id+"F1.wireOp",EDGE,"E2.8.0.0"),sQuery(id+"F1.wireOp",EDGE,"E2.8.0.1"),sQuery(id+"F1.wireOp",EDGE,"E2.8.0.3"),sQuery(id+"F1.wireOp",EDGE,"E2.9.0.0"),sQuery(id+"F1.wireOp",EDGE,"E2.9.0.1"),sQuery(id+"F1.wireOp",EDGE,"E2.9.0.3"),sQuery(id+"F1.wireOp",EDGE,"E3.bottom"),sQuery(id+"F1.wireOp",EDGE,"E3.top"),sQuery(id+"F1.wireOp",EDGE,"E3.left"),sQuery(id+"F1.wireOp",EDGE,"E3.right")])]}),"instanceName":"1"});
            var Q1;
            Q1=makeQuery(id+"F9.opPattern","COPY",BODY,{"derivedFrom":makeQuery(id+"F5.opPattern","COPY",BODY,{"derivedFrom":makeQuery(id+"F4.opExtrude","SWEPT_BODY",BODY,{"disambiguationData":[OSD([sQuery(id+"F3.wireOp",EDGE,"E4.bottom"),sQuery(id+"F3.wireOp",EDGE,"E4.left"),sQuery(id+"F3.wireOp",EDGE,"E4.right"),sQuery(id+"F3.wireOp",EDGE,"E5.1.0.1"),sQuery(id+"F3.wireOp",EDGE,"E5.1.0.2"),sQuery(id+"F3.wireOp",EDGE,"E5.1.0.3"),sQuery(id+"F3.wireOp",EDGE,"E5.2.0.1"),sQuery(id+"F3.wireOp",EDGE,"E5.2.0.2"),sQuery(id+"F3.wireOp",EDGE,"E5.2.0.3"),sQuery(id+"F3.wireOp",EDGE,"E5.3.0.1"),sQuery(id+"F3.wireOp",EDGE,"E5.3.0.2"),sQuery(id+"F3.wireOp",EDGE,"E5.3.0.3"),sQuery(id+"F3.wireOp",EDGE,"E5.4.0.1"),sQuery(id+"F3.wireOp",EDGE,"E5.4.0.2"),sQuery(id+"F3.wireOp",EDGE,"E5.4.0.3"),sQuery(id+"F3.wireOp",EDGE,"E5.5.0.1"),sQuery(id+"F3.wireOp",EDGE,"E5.5.0.2"),sQuery(id+"F3.wireOp",EDGE,"E5.5.0.3"),sQuery(id+"F3.wireOp",EDGE,"E5.6.0.1"),sQuery(id+"F3.wireOp",EDGE,"E5.6.0.2"),sQuery(id+"F3.wireOp",EDGE,"E5.6.0.3"),sQuery(id+"F3.wireOp",EDGE,"E5.7.0.1"),sQuery(id+"F3.wireOp",EDGE,"E5.7.0.2"),sQuery(id+"F3.wireOp",EDGE,"E5.7.0.3"),sQuery(id+"F3.wireOp",EDGE,"E5.8.0.1"),sQuery(id+"F3.wireOp",EDGE,"E5.8.0.2"),sQuery(id+"F3.wireOp",EDGE,"E5.8.0.3"),sQuery(id+"F3.wireOp",EDGE,"E5.9.0.1"),sQuery(id+"F3.wireOp",EDGE,"E5.9.0.2"),sQuery(id+"F3.wireOp",EDGE,"E5.9.0.3"),sQuery(id+"F3.wireOp",EDGE,"E6.1.0.0"),sQuery(id+"F3.wireOp",EDGE,"E6.1.0.1"),sQuery(id+"F3.wireOp",EDGE,"E6.1.0.3"),sQuery(id+"F3.wireOp",EDGE,"E6.2.0.0"),sQuery(id+"F3.wireOp",EDGE,"E6.2.0.1"),sQuery(id+"F3.wireOp",EDGE,"E6.2.0.3"),sQuery(id+"F3.wireOp",EDGE,"E6.3.0.0"),sQuery(id+"F3.wireOp",EDGE,"E6.3.0.1"),sQuery(id+"F3.wireOp",EDGE,"E6.3.0.3"),sQuery(id+"F3.wireOp",EDGE,"E6.4.0.0"),sQuery(id+"F3.wireOp",EDGE,"E6.4.0.1"),sQuery(id+"F3.wireOp",EDGE,"E6.4.0.3"),sQuery(id+"F3.wireOp",EDGE,"E6.5.0.0"),sQuery(id+"F3.wireOp",EDGE,"E6.5.0.1"),sQuery(id+"F3.wireOp",EDGE,"E6.5.0.3"),sQuery(id+"F3.wireOp",EDGE,"E6.6.0.0"),sQuery(id+"F3.wireOp",EDGE,"E6.6.0.1"),sQuery(id+"F3.wireOp",EDGE,"E6.6.0.3"),sQuery(id+"F3.wireOp",EDGE,"E6.7.0.0"),sQuery(id+"F3.wireOp",EDGE,"E6.7.0.1"),sQuery(id+"F3.wireOp",EDGE,"E6.7.0.3"),sQuery(id+"F3.wireOp",EDGE,"E6.8.0.0"),sQuery(id+"F3.wireOp",EDGE,"E6.8.0.1"),sQuery(id+"F3.wireOp",EDGE,"E6.8.0.3"),sQuery(id+"F3.wireOp",EDGE,"E6.9.0.0"),sQuery(id+"F3.wireOp",EDGE,"E6.9.0.1"),sQuery(id+"F3.wireOp",EDGE,"E6.9.0.3"),sQuery(id+"F3.wireOp",EDGE,"E7.bottom"),sQuery(id+"F3.wireOp",EDGE,"E7.top"),sQuery(id+"F3.wireOp",EDGE,"E7.left"),sQuery(id+"F3.wireOp",EDGE,"E7.right")])]}),"instanceName":"1"}),"instanceName":"1"});
            var Q2;
            Q2=makeQuery(id+"F2.opExtrude","CAP_EDGE",EDGE,{"disambiguationData":[OSD([sQuery(id+"F1.wireOp",EDGE,"E3.top")])],"isStart":true});
            var Q3;
            Q3=qCreatedBy(makeId("Right.planeOp"),FACE);
            transform(context, id + "F10", {"entities" : qUnion([Q0, Q1]), "transformType" : TransformType.TRANSLATION_DISTANCE, "transformDirection" : qUnion([Q3]), "distance" : 37 * mm, "makeCopy" : false});
        }
        {
            var Q0;
            Q0=qCreatedBy(makeId("Top.planeOp"),FACE);
            var sketch = newSketch(context, id + "F11", { "sketchPlane" : qUnion([Q0])});
            skLineSegment(sketch, "E9", {"start": v(25, -1.9) * mm, "end": v(25, 10) * mm});
            skLineSegment(sketch, "E10", {"start": v(25, 10) * mm, "end": v(22.1, 10) * mm});
            skLineSegment(sketch, "E11", {"start": v(22.1, 10) * mm, "end": v(22.1, 9) * mm});
            skLineSegment(sketch, "E12", {"start": v(22.1, 9) * mm, "end": v(24, 9) * mm});
            skLineSegment(sketch, "E13", {"start": v(24, 9) * mm, "end": v(24, -1.9) * mm});
            skLineSegment(sketch, "E14", {"start": v(24, -1.9) * mm, "end": v(25, -1.9) * mm});
            skSolve(sketch);
        }
        {
            var Q0;
            Q0=qSketchRegion(id+"F11",true);
            extrude(context, id + "F12", {"entities" : qUnion([Q0]), "operationType" : NewBodyOperationType.ADD, "depth" : (getVariable(context, 'pegThickness')) * mm});
        }
        {
            var Q0;
            Q0=qCreatedBy(makeId("Top.planeOp"),FACE);
            var sketch = newSketch(context, id + "F13", { "sketchPlane" : qUnion([Q0])});
            skLineSegment(sketch, "E15", {"start": v(-23, -1) * mm, "end": v(-23, 12) * mm});
            skLineSegment(sketch, "E16", {"start": v(-23, 12) * mm, "end": v(27, 12) * mm});
            skLineSegment(sketch, "E17", {"start": v(27, 12) * mm, "end": v(27, -47) * mm});
            skLineSegment(sketch, "E18", {"start": v(27, -47) * mm, "end": v(14, -47) * mm});
            skLineSegment(sketch, "E19", {"start": v(14, -47) * mm, "end": v(14, -1) * mm});
            skLineSegment(sketch, "E20", {"start": v(14, -1) * mm, "end": v(-23, -1) * mm});
            skSolve(sketch);
        }
        {
            var Q0;
            Q0=qSketchRegion(id+"F13",true);
            extrude(context, id + "F14", {"entities" : qUnion([Q0]), "operationType" : NewBodyOperationType.ADD, "oppositeDirection" : true, "depth" : 0.2 * mm});
        }
    });
